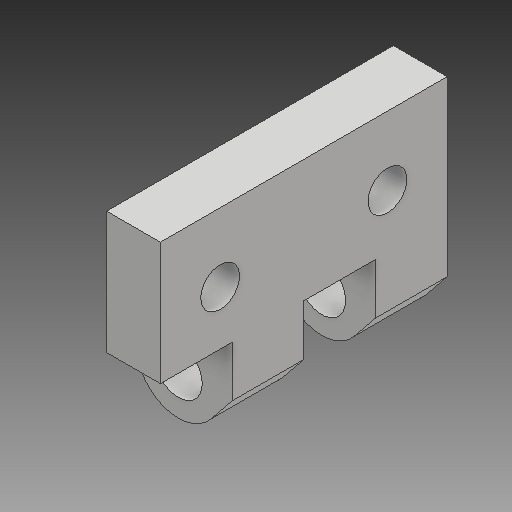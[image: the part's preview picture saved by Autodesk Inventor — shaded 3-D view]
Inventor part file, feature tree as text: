
AUTODESK INVENTOR PART (.ipt)
format: ipt  version: 2018 (Build 220112000, 112)  size: 150,016 bytes
history: native  units: mm
features: sketch x3, extrude x2, projected_geometry x2, hole x1
ambient origin geometry x8: Origin, YZ Plane, XZ Plane, XY Plane, X Axis, Y Axis, Z Axis, Center Point
bodies: Volumenkörper1 (feature_tree)
feature tree (8):
  extrude  "Extrusion1"  Depth=0.9mm
  extrude  "Extrusion2"  Depth=2.9mm
  hole  "Bohrung2"  [1 undecoded]
  sketch  "Skizze1"  dims[d0=0.9mm d2=0.8mm]
  sketch  "Skizze2"  dims[d3=1.4mm d4=2.9mm]
  projected_geometry  "Projizierte Kontur1"
  sketch  "Skizze4"  dims[d5=4.8mm d6=0.0mm d7=0.85mm d8=2.0mm d9=1.2mm d10=1.2mm d11=1.2mm d12=4.0mm d13=0.0mm d23=0.65mm d24=6.0mm d25=1.0mm d26=2.0mm d27=90.0deg d28=8.0mm d29=20.594885mm d30=2.8mm d31=1.15mm]
  projected_geometry  "Projizierte Kontur3"
note: 1 required parameter value undecoded (feature->parameter linkage not recoverable at this tier; creation-order binding heuristic only, values carry confidence <= 0.55)
